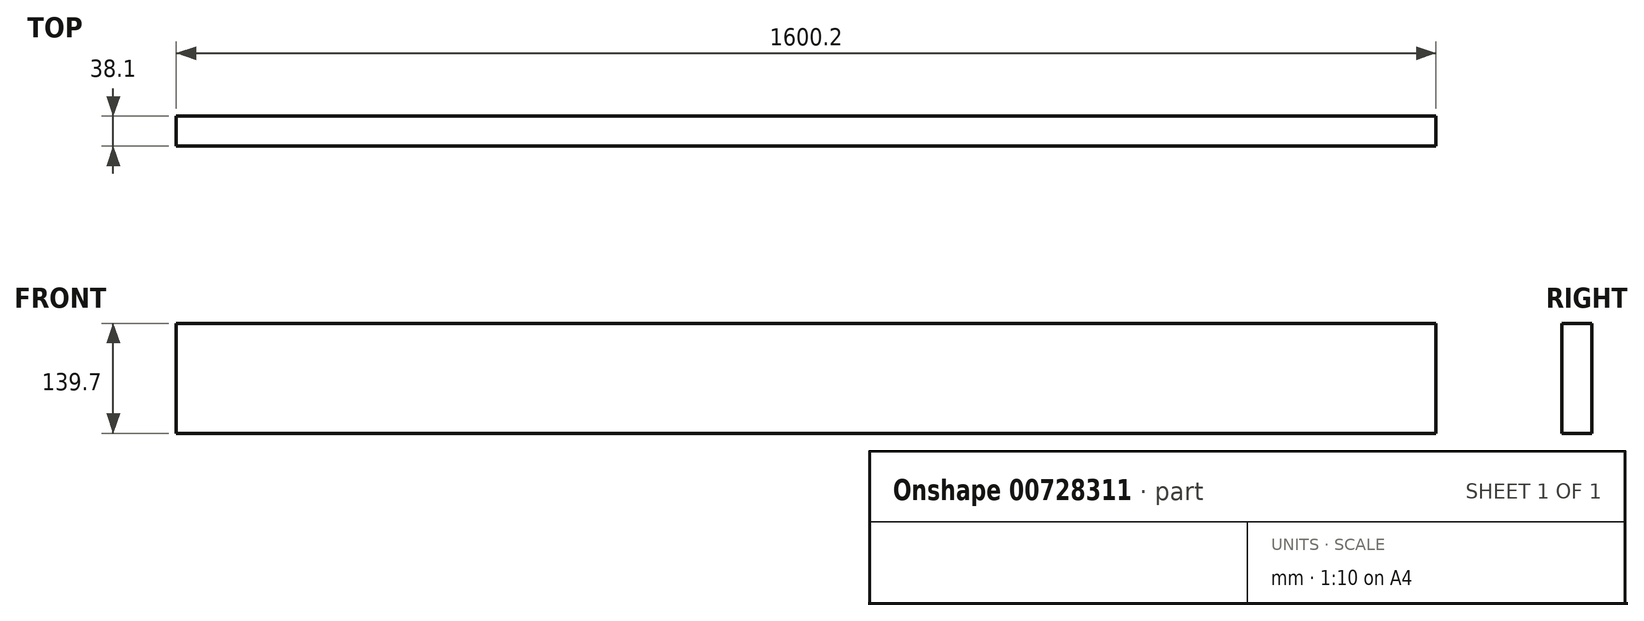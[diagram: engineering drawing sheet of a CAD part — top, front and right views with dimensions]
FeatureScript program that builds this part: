
annotation { "Feature Type Name" : "Feature", "Feature Type Description" : "" }
export const myFeature = defineFeature(function(context is Context, id is Id, definition is map)
    precondition{}
    {
        {
            var Q0;
            Q0=qCreatedBy(makeId("Front.planeOp"),FACE);
            var sketch = newSketch(context, id + "F0", { "sketchPlane" : qUnion([Q0])});
            skLineSegment(sketch, "E0.bottom", {"start": v(-800.1, -69.85) * mm, "end": v(800.1, -69.85) * mm});
            skLineSegment(sketch, "E0.top", {"start": v(-800.1, 69.85) * mm, "end": v(800.1, 69.85) * mm});
            skLineSegment(sketch, "E0.left", {"start": v(-800.1, -69.85) * mm, "end": v(-800.1, 69.85) * mm});
            skLineSegment(sketch, "E0.right", {"start": v(800.1, -69.85) * mm, "end": v(800.1, 69.85) * mm});
            skPoint(sketch, "E0.middle", {"position": v(0, 0) * mm});
            skSolve(sketch);
        }
        {
            var Q0;
            Q0=qSketchRegion(id+"F0",true);
            extrude(context, id + "F1", {"entities" : qUnion([Q0]), "depth" : 38.1 * mm});
        }
    });
